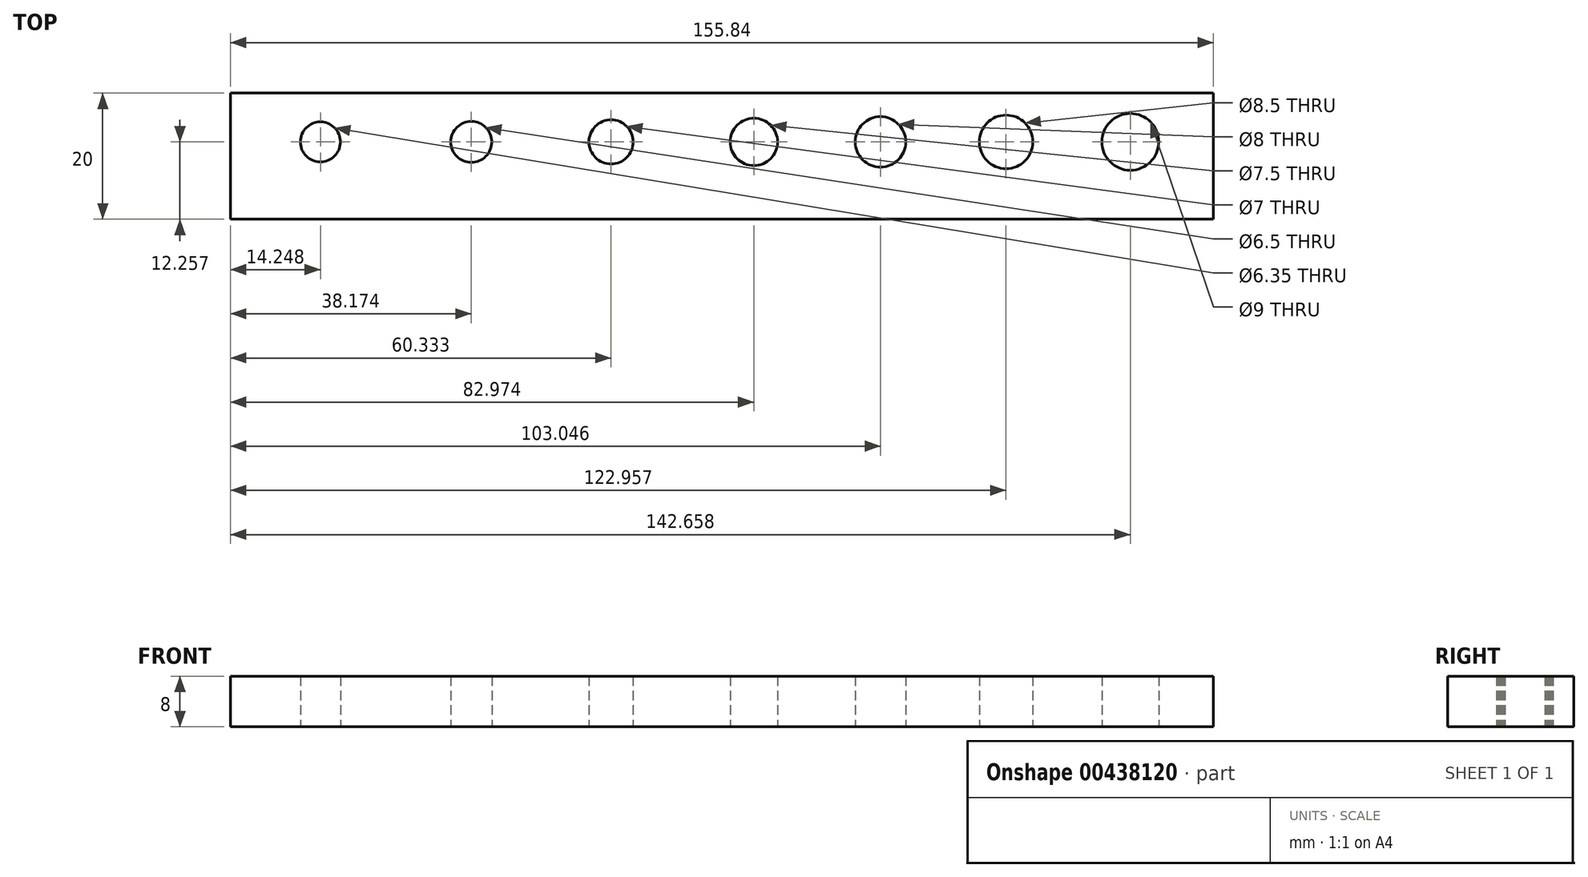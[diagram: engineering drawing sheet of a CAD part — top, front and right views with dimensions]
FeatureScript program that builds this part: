
annotation { "Feature Type Name" : "Feature", "Feature Type Description" : "" }
export const myFeature = defineFeature(function(context is Context, id is Id, definition is map)
    precondition{}
    {
        {
            var Q0;
            Q0=qCreatedBy(makeId("Top.planeOp"),FACE);
            var sketch = newSketch(context, id + "F0", { "sketchPlane" : qUnion([Q0])});
            skLineSegment(sketch, "E0.bottom", {"start": v(-90, 20) * mm, "end": v(65.84, 20) * mm});
            skLineSegment(sketch, "E0.left", {"start": v(-90, 20) * mm, "end": v(-90, 0) * mm});
            skPoint(sketch, "E0.middle", {"position": v(0, 0) * mm});
            skLineSegment(sketch, "E1", {"start": v(0, 20) * mm, "end": v(0, 0) * mm, "construction": true});
            skLineSegment(sketch, "E2", {"start": v(-90, 12.26) * mm, "end": v(65.84, 12.26) * mm, "construction": true});
            skPoint(sketch, "E3", {"position": v(-75.75, 12.26) * mm});
            skCircle(sketch, "E4", {"center": v(-75.75, 12.26) * mm, "radius": 3.17 * mm});
            skPoint(sketch, "E5", {"position": v(-51.83, 12.26) * mm});
            skCircle(sketch, "E6", {"center": v(-51.83, 12.26) * mm, "radius": 3.25 * mm});
            skCircle(sketch, "E7", {"center": v(-29.67, 12.26) * mm, "radius": 3.5 * mm});
            skCircle(sketch, "E8", {"center": v(-7.03, 12.26) * mm, "radius": 3.75 * mm});
            skCircle(sketch, "E9", {"center": v(13.05, 12.26) * mm, "radius": 4 * mm});
            skCircle(sketch, "E10", {"center": v(32.96, 12.26) * mm, "radius": 4.25 * mm});
            skLineSegment(sketch, "E11", {"start": v(-90, 0) * mm, "end": v(65.84, 0) * mm});
            skPoint(sketch, "E12.orphan", {"position": v(0, -20) * mm});
            skPoint(sketch, "E13.orphan", {"position": v(-90, -20) * mm});
            skPoint(sketch, "E14.orphan", {"position": v(90, -20) * mm});
            skCircle(sketch, "E15", {"center": v(52.66, 12.26) * mm, "radius": 4.5 * mm});
            skLineSegment(sketch, "E16", {"start": v(65.84, 20) * mm, "end": v(65.84, 0) * mm});
            skPoint(sketch, "E17.orphan", {"position": v(90, 0) * mm});
            skPoint(sketch, "E0.right.start.orphan", {"position": v(90, 20) * mm});
            skSolve(sketch);
        }
        {
            var Q0;
            Q0=makeQuery(id+"F0.imprint","IMPRINT",FACE,{"disambiguationData":[TD([[makeQuery(id+"F0.imprint","IMPRINT",EDGE,{"derivedFrom":sQuery(id+"F0.wireOp",EDGE,"E0.bottom")}),-1.0]])]});
            extrude(context, id + "F1", {"entities" : qUnion([Q0]), "depth" : 8 * mm, "offsetDistance" : 25 * mm});
        }
    });
